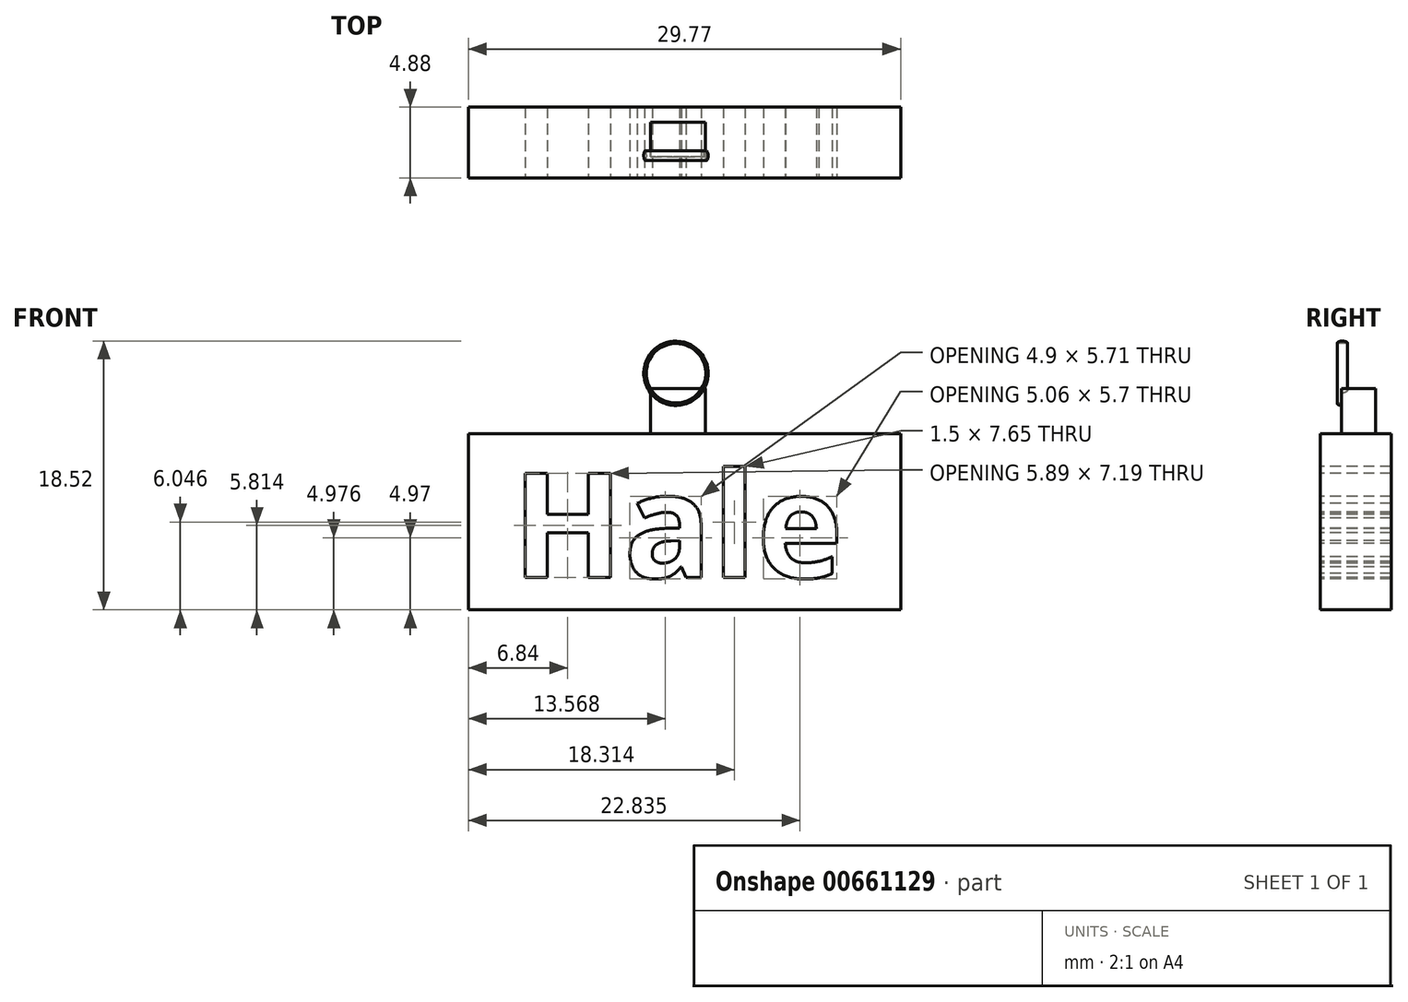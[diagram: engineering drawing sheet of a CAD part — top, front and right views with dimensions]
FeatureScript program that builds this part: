
annotation { "Feature Type Name" : "Feature", "Feature Type Description" : "" }
export const myFeature = defineFeature(function(context is Context, id is Id, definition is map)
    precondition{}
    {
        {
            var Q0;
            Q0=qCreatedBy(makeId("Front.planeOp"),FACE);
            var sketch = newSketch(context, id + "F0", { "sketchPlane" : qUnion([Q0])});
            skLineSegment(sketch, "E0.bottom", {"start": v(-69.68, 66.45) * mm, "end": v(-39.91, 66.45) * mm});
            skLineSegment(sketch, "E0.top", {"start": v(-69.68, 54.32) * mm, "end": v(-39.91, 54.32) * mm});
            skLineSegment(sketch, "E0.left", {"start": v(-69.68, 66.45) * mm, "end": v(-69.68, 54.32) * mm});
            skLineSegment(sketch, "E0.right", {"start": v(-39.91, 66.45) * mm, "end": v(-39.91, 54.32) * mm});
            skSolve(sketch);
        }
        {
            var Q0;
            Q0=makeQuery(id+"F0.imprint","IMPRINT",FACE,{"disambiguationData":[TD([[makeQuery(id+"F0.imprint","IMPRINT",EDGE,{"derivedFrom":sQuery(id+"F0.wireOp",EDGE,"E0.bottom")}),-1.0]])]});
            extrude(context, id + "F1", {"entities" : qUnion([Q0]), "oppositeDirection" : true, "depth" : 4.88 * mm, "offsetDistance" : 25.4 * mm});
        }
        {
            var Q0;
            Q0=makeQuery(id+"F1.opExtrude","CAP_FACE",FACE,{"disambiguationData":[OSD([sQuery(id+"F0.wireOp",EDGE,"E0.bottom"),sQuery(id+"F0.wireOp",EDGE,"E0.top"),sQuery(id+"F0.wireOp",EDGE,"E0.left"),sQuery(id+"F0.wireOp",EDGE,"E0.right")])],"isStart":true});
            var sketch = newSketch(context, id + "F2", { "sketchPlane" : qUnion([Q0])});
            skText(sketch, "E1", { "text": "Hale", "fontName": "OpenSans-Bold.ttf"});
            const initialGuessF2  = {"E1": [-0.06669, 0.05654, 1, 0, 0.00725]};
            skSetInitialGuess(sketch, initialGuessF2);
            skSolve(sketch);
        }
        {
            var Q0;
            Q0=makeQuery(id+"F1.opExtrude","SWEPT_FACE",FACE,{"disambiguationData":[OSD([sQuery(id+"F0.wireOp",EDGE,"E0.bottom")])]});
            var sketch = newSketch(context, id + "F3", { "sketchPlane" : qUnion([Q0])});
            skLineSegment(sketch, "E2.bottom", {"start": v(-53.35, 1.46) * mm, "end": v(-57.15, 1.46) * mm});
            skLineSegment(sketch, "E2.top", {"start": v(-53.35, 3.83) * mm, "end": v(-57.15, 3.83) * mm});
            skLineSegment(sketch, "E2.left", {"start": v(-53.35, 1.46) * mm, "end": v(-53.35, 3.83) * mm});
            skLineSegment(sketch, "E2.right", {"start": v(-57.15, 1.46) * mm, "end": v(-57.15, 3.83) * mm});
            skPoint(sketch, "E2.middle", {"position": v(-55.25, 2.64) * mm});
            skSolve(sketch);
        }
        {
            var Q0;
            Q0=makeQuery(id+"F3.imprint","IMPRINT",FACE,{"disambiguationData":[TD([[makeQuery(id+"F3.imprint","IMPRINT",EDGE,{"derivedFrom":sQuery(id+"F3.wireOp",EDGE,"E2.bottom")}),-1.0]])]});
            extrude(context, id + "F4", {"entities" : qUnion([Q0]), "operationType" : NewBodyOperationType.ADD, "depth" : 3.1 * mm, "offsetDistance" : 25.4 * mm});
        }
        {
            var Q0;
            Q0=makeQuery(id+"F4.opExtrude","SWEPT_FACE",FACE,{"disambiguationData":[OSD([sQuery(id+"F3.wireOp",EDGE,"E2.bottom")])]});
            var sketch = newSketch(context, id + "F5", { "sketchPlane" : qUnion([Q0])});
            skCircle(sketch, "E3", {"center": v(-55.4, 70.62) * mm, "radius": 2.39 * mm});
            skSolve(sketch);
        }
        {
            var Q0;
            Q0=makeQuery(id+"F4.opExtrude","SWEPT_FACE",FACE,{"disambiguationData":[OSD([sQuery(id+"F3.wireOp",EDGE,"E2.left")])]});
            var sketch = newSketch(context, id + "F6", { "sketchPlane" : qUnion([Q0])});
            skCircle(sketch, "E4", {"center": v(1.52, 71.14) * mm, "radius": 0.35 * mm});
            skSolve(sketch);
        }
        {
            var Q0;
            Q0=makeQuery(id+"F6.imprint","IMPRINT",FACE,{"disambiguationData":[TD([[makeQuery(id+"F6.imprint","IMPRINT",EDGE,{"derivedFrom":sQuery(id+"F6.wireOp",EDGE,"E4")}),1.0]])]});
            var Q1;
            Q1=sQuery(id+"F5.wireOp",EDGE,"E3");
            sweep(context, id + "F7", {"operationType" : NewBodyOperationType.ADD, "profiles" : qUnion([Q0]), "path" : qUnion([Q1])});
        }
        {
            var Q0;
            Q0=makeQuery(id+"F2.imprint","IMPRINT",FACE,{"disambiguationData":[TD([[makeQuery(id+"F2.imprint","IMPRINT",EDGE,{"derivedFrom":sQuery(id+"F2.wireOp",EDGE,"E1.sketch_text.stroke-0")}),-1.0]])]});
            var Q1;
            Q1=makeQuery(id+"F2.imprint","IMPRINT",FACE,{"disambiguationData":[TD([[makeQuery(id+"F2.imprint","IMPRINT",EDGE,{"derivedFrom":sQuery(id+"F2.wireOp",EDGE,"E1.sketch_text.stroke-12")}),-1.0]])]});
            var Q2;
            Q2=makeQuery(id+"F2.imprint","IMPRINT",FACE,{"disambiguationData":[TD([[makeQuery(id+"F2.imprint","IMPRINT",EDGE,{"derivedFrom":sQuery(id+"F2.wireOp",EDGE,"E1.sketch_text.stroke-37")}),-1.0]])]});
            var Q3;
            Q3=makeQuery(id+"F2.imprint","IMPRINT",FACE,{"disambiguationData":[TD([[makeQuery(id+"F2.imprint","IMPRINT",EDGE,{"derivedFrom":sQuery(id+"F2.wireOp",EDGE,"E1.sketch_text.stroke-41")}),-1.0]])]});
            extrude(context, id + "F8", {"entities" : qUnion([Q0, Q1, Q2, Q3]), "operationType" : NewBodyOperationType.REMOVE, "oppositeDirection" : true, "depth" : 25.4 * mm, "offsetDistance" : 25.4 * mm});
        }
    });
